# Revit family: Sanitary_Mirrors_hansgrohe_73570CHN-Logis-Universal-Shaving-mirror
name_source: partatom
category: Furniture
revit_build: Autodesk Revit 2018 (Build: 20190510_1515(x64)
units: mm (PartAtom-declared; Revit-internal decimal feet)

## family parameters
Always vertical = No
Cut with Voids When Loaded = No
OmniClass Number = 23.21.37.13.15
OmniClass Title = Mirrors
Room Calculation Point = No
Shared = No
Work Plane-Based = Yes

## types (1)
- 007 Chrome
    Always visible = Yes
    BIMobject category = Mirrors
    Default Elevation = 1219.2 mm  [stored 4 ft]
    Description = Logis Universal Shaving mirror with LED light
    Edition number = 1
    IFC Classification = Electric Appliance
    Lamp material = Hansgrohe - Plastic - White
    Main material = Hansgrohe - Metal - 007 Chrome
    Manufacturer = Hansgrohe
    Manufacturer name = hansgrohe
    Mirror material = Hansgrohe - Glass - Mirror
    Model = 73570CHN
    OmniClass Code = 23-21 37 13 15
    OmniClass Description = Mirrors
    Product Guid = 7fb2a505-f41a-434e-a916-86995c17ab0c
    Product SKU = 73570CHN
    Product data url = https://bimobject.com
    Product family = Logis Universal
    Product group = Mirrors
    Product name = 73570CHN Logis Universal Shaving mirror with LED light
    Product url = https://www.hansgrohe.com
    QR code = https://bimobject.com
    Switch material = Hansgrohe - Plastic - Black
    URL = https://www.hansgrohe.com
    Voltage = 240 V
    Weight Net (Kg) = 1.5

note: [stored X ft] marks values corroborated as IEEE doubles in the binary element streams (Revit-internal decimal feet)

## geometry (parser evidence)
native form markers: Sweep x3
no freeform markers — native parametric forms only
